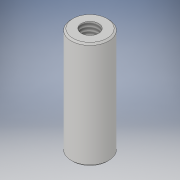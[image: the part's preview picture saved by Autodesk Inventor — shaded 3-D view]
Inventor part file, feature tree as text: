
AUTODESK INVENTOR PART (.ipt)
format: ipt  version: 2018 (Build 220112000, 112)  size: 105,472 bytes
history: native  units: mm
features: extrude x1, chamfer x1, hole x1, sketch x1
ambient origin geometry x8: Origin, YZ Plane, XZ Plane, XY Plane, X Axis, Y Axis, Z Axis, Center Point
bodies: Volumenkörper1 (feature_tree)
feature tree (4):
  extrude  "Extrusion1"  Depth=20.0mm
  chamfer  "Fase1"  [1 undecoded]
  hole  "Bohrung1"  [1 undecoded]
  sketch  "Skizze1"  dims[d0=7.0mm d1=20.0mm d2=0.0mm d3=0.3mm d4=2.0mm d5=45.0deg d15=10.0mm d16=10.0mm d8=3.242mm d9=20.0mm d10=4.0mm d11=2.0mm d12=90.0deg d13=11.8mm d14=20.594885mm]
note: 2 required parameter values undecoded (feature->parameter linkage not recoverable at this tier; creation-order binding heuristic only, values carry confidence <= 0.55)
